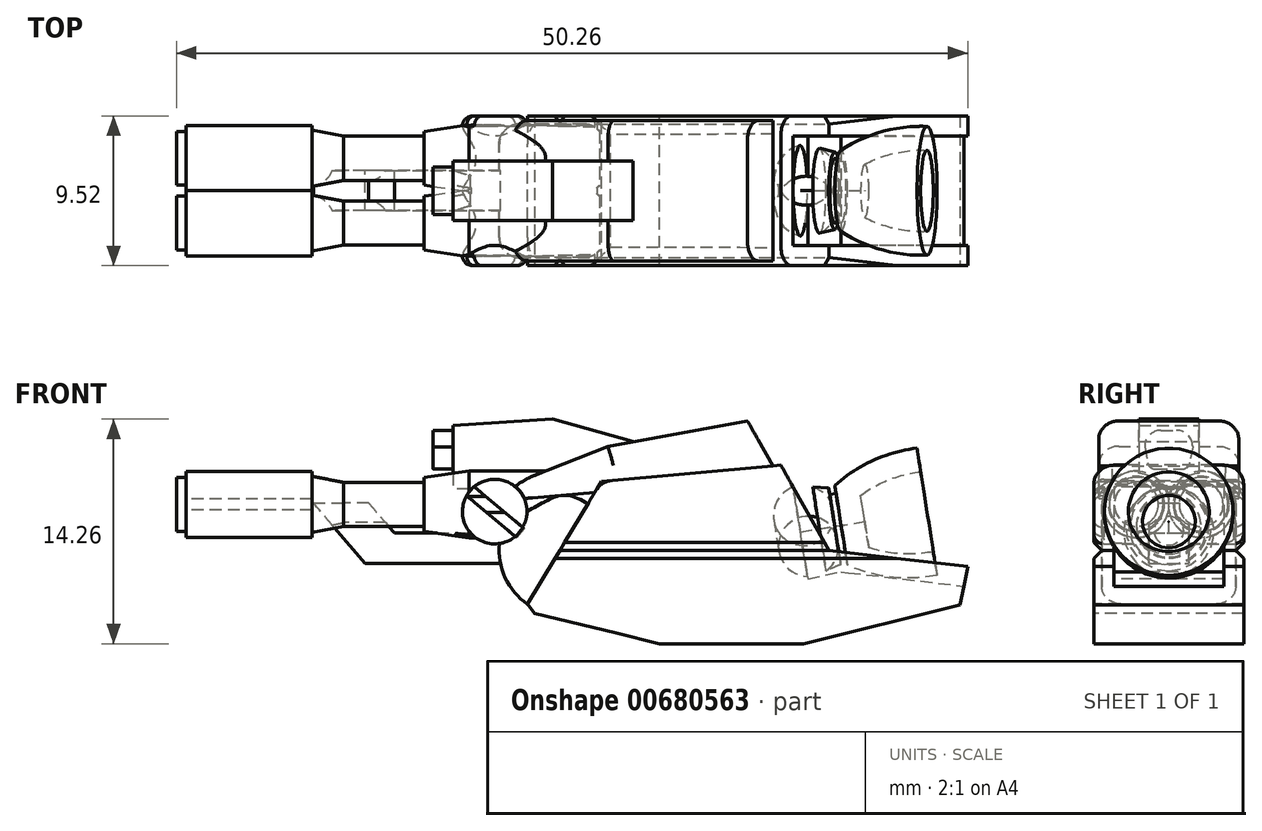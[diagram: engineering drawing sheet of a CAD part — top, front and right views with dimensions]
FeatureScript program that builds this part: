
annotation { "Feature Type Name" : "Feature", "Feature Type Description" : "" }
export const myFeature = defineFeature(function(context is Context, id is Id, definition is map)
    precondition{}
    {
        {
            var Q0;
            Q0=qCreatedBy(makeId("Front.planeOp"),FACE);
            var sketch = newSketch(context, id + "F0", { "sketchPlane" : qUnion([Q0])});
            skLineSegment(sketch, "E0", {"start": v(0, 0) * mm, "end": v(1.5, 0.24) * mm, "construction": true});
            skLineSegment(sketch, "E1", {"start": v(0, 0) * mm, "end": v(-2.23, 14.05) * mm, "construction": true});
            skLineSegment(sketch, "E2", {"start": v(5.05, 3.4) * mm, "end": v(4.82, 4.9) * mm});
            skLineSegment(sketch, "E3", {"start": v(-0.32, 2.02) * mm, "end": v(-0.4, 2.53) * mm});
            skArc(sketch, "E4", {"start": v(4.82, 4.9) * mm, "mid": v(2.02, 4.12) * mm, "end": v(-0.4, 2.53) * mm});
            skLineSegment(sketch, "E5", {"start": v(0, 0) * mm, "end": v(-19.66, -3.11) * mm, "construction": true});
            skLineSegment(sketch, "E6", {"start": v(-0.32, 2.02) * mm, "end": v(-0.72, 1.96) * mm});
            skLineSegment(sketch, "E7", {"start": v(-0.72, 1.96) * mm, "end": v(-0.79, 2.36) * mm});
            skLineSegment(sketch, "E8", {"start": v(-0.79, 2.36) * mm, "end": v(-1.8, 2.45) * mm});
            skLineSegment(sketch, "E9", {"start": v(-0.79, 2.36) * mm, "end": v(-6.83, 1.4) * mm, "construction": true});
            skLineSegment(sketch, "E10", {"start": v(-3.63, 6.1) * mm, "end": v(-2.98, 2.02) * mm, "construction": true});
            skLineSegment(sketch, "E11", {"start": v(-1.8, 2.45) * mm, "end": v(-3.02, 2.26) * mm, "construction": true});
            skPoint(sketch, "E12", {"position": v(-3.05, 2.42) * mm});
            skArc(sketch, "E13", {"start": v(-1.8, 2.45) * mm, "mid": v(-2.43, 2.54) * mm, "end": v(-3.05, 2.42) * mm});
            skLineSegment(sketch, "E14", {"start": v(-3.05, 2.42) * mm, "end": v(-2.6, -0.41) * mm});
            skLineSegment(sketch, "E15", {"start": v(-2.6, -0.41) * mm, "end": v(1.5, 0.24) * mm});
            skArc(sketch, "E16", {"start": v(5.05, 3.4) * mm, "mid": v(3.05, 2.9) * mm, "end": v(1.24, 1.9) * mm});
            skLineSegment(sketch, "E17", {"start": v(1.24, 1.9) * mm, "end": v(1.5, 0.24) * mm});
            skLineSegment(sketch, "E18.trimOffspring", {"start": v(5.46, 0.86) * mm, "end": v(24.57, 3.9) * mm, "construction": true});
            skSolve(sketch);
        }
        {
            var Q0;
            Q0=makeQuery(id+"F0.imprint","IMPRINT",FACE,{"disambiguationData":[TD([[makeQuery(id+"F0.imprint","IMPRINT",EDGE,{"derivedFrom":sQuery(id+"F0.wireOp",EDGE,"E2")}),1.0]])]});
            var Q1;
            Q1=sQuery(id+"F0.wireOp",EDGE,"E5");
            revolve(context, id + "F1", {"entities" : qUnion([Q0]), "axis" : qUnion([Q1]), "revolveType" : RevolveType.FULL});
        }
        {
            var Q0;
            Q0=qCreatedBy(makeId("Front.planeOp"),FACE);
            var sketch = newSketch(context, id + "F2", { "sketchPlane" : qUnion([Q0])});
            skLineSegment(sketch, "E19", {"start": v(0, 0) * mm, "end": v(1.56, -9.86) * mm, "construction": true});
            skLineSegment(sketch, "E20", {"start": v(0.48, -3.01) * mm, "end": v(7.8, -3.87) * mm});
            skLineSegment(sketch, "E21", {"start": v(7.8, -3.87) * mm, "end": v(7.55, -5.07) * mm});
            skLineSegment(sketch, "E22", {"start": v(7.55, -5.07) * mm, "end": v(-2.39, -7.52) * mm});
            skLineSegment(sketch, "E23", {"start": v(-2.39, -7.52) * mm, "end": v(-14.3, -6.85) * mm});
            skLineSegment(sketch, "E24", {"start": v(-15.66, 2.07) * mm, "end": v(-15.25, 2.78) * mm});
            skLineSegment(sketch, "E25", {"start": v(-15.25, 2.78) * mm, "end": v(-3.83, 3.82) * mm});
            skLineSegment(sketch, "E26", {"start": v(0.48, -3.01) * mm, "end": v(0, -2.95) * mm});
            skLineSegment(sketch, "E27", {"start": v(-3.83, 3.82) * mm, "end": v(-3.05, 2.44) * mm});
            skLineSegment(sketch, "E28", {"start": v(0, -2.95) * mm, "end": v(-50.8, -2.95) * mm, "construction": true});
            skLineSegment(sketch, "E29", {"start": v(-19.92, -5) * mm, "end": v(-19.48, -5.6) * mm});
            skLineSegment(sketch, "E30", {"start": v(-19.48, -5.6) * mm, "end": v(-14.3, -6.85) * mm});
            skLineSegment(sketch, "E31", {"start": v(-3.05, 2.44) * mm, "end": v(-2.12, -3.4) * mm});
            skLineSegment(sketch, "E32", {"start": v(-2.12, -3.4) * mm, "end": v(0, -2.95) * mm});
            skLineSegment(sketch, "E33", {"start": v(-2.12, -3.4) * mm, "end": v(-2.12, 15.55) * mm, "construction": true});
            skLineSegment(sketch, "E34", {"start": v(-15.66, 2.07) * mm, "end": v(-19.92, -5) * mm});
            skPoint(sketch, "E35.end.orphan", {"position": v(-34.01, 0.4) * mm});
            skPoint(sketch, "E36.orphan", {"position": v(-35.04, -0.28) * mm});
            skPoint(sketch, "E37.start.orphan", {"position": v(-32.58, -4.06) * mm});
            skSolve(sketch);
        }
        {
            var Q0;
            Q0=qSketchRegion(id+"F2",true);
            extrude(context, id + "F3", {"entities" : qUnion([Q0]), "operationType" : NewBodyOperationType.ADD, "endBound" : BoundingType.SYMMETRIC, "oppositeDirection" : true, "depth" : 9.52 * mm, "offsetDistance" : 25.4 * mm});
        }
        {
            var Q0;
            Q0=makeQuery(id+"F3.opExtrude","CAP_FACE",FACE,{"disambiguationData":[OSD([sQuery(id+"F2.wireOp",EDGE,"E20"),sQuery(id+"F2.wireOp",EDGE,"E21"),sQuery(id+"F2.wireOp",EDGE,"E22"),sQuery(id+"F2.wireOp",EDGE,"E23"),sQuery(id+"F2.wireOp",EDGE,"6j32zmyG-TKOO-vOuO-Pmrx-HYvCCri2Y5XP"),sQuery(id+"F2.wireOp",EDGE,"E37"),sQuery(id+"F2.wireOp",EDGE,"E35"),sQuery(id+"F2.wireOp",EDGE,"kUpx39iX-orTo-v9rc-2KpO-4MKOgX1ehOD6"),sQuery(id+"F2.wireOp",EDGE,"E24"),sQuery(id+"F2.wireOp",EDGE,"E25"),sQuery(id+"F2.wireOp",EDGE,"E26"),sQuery(id+"F2.wireOp",EDGE,"E27"),sQuery(id+"F2.wireOp",EDGE,"E29"),sQuery(id+"F2.wireOp",EDGE,"E30"),sQuery(id+"F2.wireOp",EDGE,"E31"),sQuery(id+"F2.wireOp",EDGE,"E32")])],"isStart":true});
            var sketch = newSketch(context, id + "F4", { "sketchPlane" : qUnion([Q0])});
            skLineSegment(sketch, "E38", {"start": v(7.8, -3.87) * mm, "end": v(8.05, -2.62) * mm});
            skLineSegment(sketch, "E39", {"start": v(8.05, -2.62) * mm, "end": v(-0.77, -1.59) * mm});
            skLineSegment(sketch, "E40", {"start": v(-3.05, 2.44) * mm, "end": v(-2.12, -3.4) * mm});
            skLineSegment(sketch, "E41", {"start": v(-2.12, -3.4) * mm, "end": v(0, -2.95) * mm});
            skLineSegment(sketch, "E42", {"start": v(0, -2.95) * mm, "end": v(7.8, -3.87) * mm});
            skLineSegment(sketch, "E43", {"start": v(-3.05, 2.44) * mm, "end": v(0, -2.95) * mm, "construction": true});
            skLineSegment(sketch, "E44", {"start": v(-3.05, 2.44) * mm, "end": v(-0.77, -1.59) * mm});
            skSolve(sketch);
        }
        {
            var Q0;
            Q0=qSketchRegion(id+"F4",true);
            extrude(context, id + "F5", {"entities" : qUnion([Q0]), "oppositeDirection" : true, "depth" : 1.27 * mm, "offsetDistance" : 25.4 * mm});
        }
        {
            var Q0;
            Q0=makeQuery(id+"F5.opExtrude","SWEPT_BODY",BODY,{"disambiguationData":[OSD([sQuery(id+"F4.wireOp",EDGE,"E38"),sQuery(id+"F4.wireOp",EDGE,"E39"),sQuery(id+"F4.wireOp",EDGE,"E40"),sQuery(id+"F4.wireOp",EDGE,"E41"),sQuery(id+"F4.wireOp",EDGE,"E42"),sQuery(id+"F4.wireOp",EDGE,"E44")])]});
            var Q1;
            Q1=qCreatedBy(makeId("Front.planeOp"),FACE);
            mirror(context, id + "F6", {"operationType" : NewBodyOperationType.ADD, "entities" : qUnion([Q0]), "mirrorPlane" : qUnion([Q1])});
        }
        {
            var Q0;
            Q0=qCreatedBy(makeId("Right.planeOp"),FACE);
            var sketch = newSketch(context, id + "F7", { "sketchPlane" : qUnion([Q0])});
            skLineSegment(sketch, "E45", {"start": v(-5.3, -1.59) * mm, "end": v(-3.08, -1.59) * mm, "construction": true});
            skLineSegment(sketch, "E46", {"start": v(-4.76, -1.53) * mm, "end": v(-4.76, -1.65) * mm, "construction": true});
            skLineSegment(sketch, "E47", {"start": v(-4.25, -1.59) * mm, "end": v(-4.82, -1.02) * mm});
            skLineSegment(sketch, "E48", {"start": v(-4.82, -1.02) * mm, "end": v(-4.82, -1.59) * mm});
            skLineSegment(sketch, "E49.MirrorCS", {"start": v(-4.82, -2.15) * mm, "end": v(-4.82, -1.59) * mm});
            skLineSegment(sketch, "E50.MirrorCS", {"start": v(-4.25, -1.59) * mm, "end": v(-4.82, -2.15) * mm});
            skLineSegment(sketch, "E51", {"start": v(0, 0) * mm, "end": v(0, -3.64) * mm, "construction": true});
            skLineSegment(sketch, "E52.MirrorCS", {"start": v(4.82, -1.02) * mm, "end": v(4.82, -1.59) * mm});
            skLineSegment(sketch, "E53.MirrorCS", {"start": v(4.82, -2.15) * mm, "end": v(4.82, -1.59) * mm});
            skLineSegment(sketch, "E54.MirrorCS", {"start": v(4.25, -1.59) * mm, "end": v(4.82, -2.15) * mm});
            skLineSegment(sketch, "E55.MirrorCS", {"start": v(4.25, -1.59) * mm, "end": v(4.82, -1.02) * mm});
            skSolve(sketch);
        }
        {
            var Q0;
            Q0=qSketchRegion(id+"F7",true);
            extrude(context, id + "F8", {"entities" : qUnion([Q0]), "operationType" : NewBodyOperationType.REMOVE, "endBound" : BoundingType.SYMMETRIC, "oppositeDirection" : true, "depth" : 50.8 * mm, "offsetDistance" : 25.4 * mm});
        }
        {
            var Q0;
            Q0=makeQuery(id+"F3.opExtrude","CAP_EDGE",EDGE,{"disambiguationData":[OSD([sQuery(id+"F2.wireOp",EDGE,"E25")])],"isStart":true});
            var Q1;
            Q1=makeQuery(id+"F3.opExtrude","CAP_EDGE",EDGE,{"disambiguationData":[OSD([sQuery(id+"F2.wireOp",EDGE,"E25")])],"isStart":false});
            var Q2;
            Q2=makeQuery(id+"F3.opExtrude","SWEPT_EDGE",EDGE,{"disambiguationData":[OSD([sQuery(id+"F2.wireOp",EDGE,"E24"),sQuery(id+"F2.wireOp",EDGE,"E25")])]});
            fillet(context, id + "F9", {"entities" : qUnion([Q0, Q1, Q2]), "radius" : 1.27 * mm, "tangentPropagation" : true, "allowEdgeOverflow" : false});
        }
        {
            var Q0;
            Q0=qCreatedBy(makeId("Front.planeOp"),FACE);
            var sketch = newSketch(context, id + "F10", { "sketchPlane" : qUnion([Q0])});
            skLineSegment(sketch, "E56", {"start": v(-19.78, 2.37) * mm, "end": v(0, 4.17) * mm, "construction": true});
            skPoint(sketch, "E57", {"position": v(-3.83, 3.82) * mm});
            skLineSegment(sketch, "E58", {"start": v(-4.72, 5.39) * mm, "end": v(1.35, -5.34) * mm, "construction": true});
            skLineSegment(sketch, "E59", {"start": v(-4.33, 3.77) * mm, "end": v(-5.95, 6.63) * mm});
            skLineSegment(sketch, "E60", {"start": v(-5.95, 6.63) * mm, "end": v(-14.81, 5.02) * mm});
            skLineSegment(sketch, "E61", {"start": v(-14.81, 5.02) * mm, "end": v(-20.9, 2.6) * mm});
            skArc(sketch, "E62", {"start": v(-20.12, 1.7) * mm, "mid": v(-20.43, 2.22) * mm, "end": v(-20.9, 2.6) * mm});
            skLineSegment(sketch, "E63", {"start": v(-20.12, 1.7) * mm, "end": v(-15.64, 2.1) * mm});
            skLineSegment(sketch, "E64", {"start": v(-15.23, 2.78) * mm, "end": v(-4.33, 3.77) * mm});
            skLineSegment(sketch, "E65", {"start": v(-15.64, 2.1) * mm, "end": v(-15.23, 2.78) * mm});
            skSolve(sketch);
        }
        {
            var Q0;
            Q0 = qSketchRegion(id + "F10", true);
            extrude(context, id + "F11", {"entities" : qUnion([Q0]), "operationType" : NewBodyOperationType.ADD, "endBound" : BoundingType.SYMMETRIC, "depth" : 8.9 * mm, "offsetDistance" : 25.4 * mm});
        }
        {
            var Q0;
            Q0=makeQuery(id+"F11.opExtrude","CAP_EDGE",EDGE,{"disambiguationData":[OSD([sQuery(id+"F10.wireOp",EDGE,"E60")])],"isStart":false});
            var Q1;
            Q1=makeQuery(id+"F11.opExtrude","CAP_EDGE",EDGE,{"disambiguationData":[OSD([sQuery(id+"F10.wireOp",EDGE,"E61")])],"isStart":false});
            var Q2;
            Q2=makeQuery(id+"F11.opExtrude","CAP_EDGE",EDGE,{"disambiguationData":[OSD([sQuery(id+"F10.wireOp",EDGE,"E61")])],"isStart":true});
            var Q3;
            Q3=makeQuery(id+"F11.opExtrude","CAP_EDGE",EDGE,{"disambiguationData":[OSD([sQuery(id+"F10.wireOp",EDGE,"E60")])],"isStart":true});
            fillet(context, id + "F12", {"entities" : qUnion([Q0, Q1, Q2, Q3]), "radius" : 1.27 * mm, "tangentPropagation" : true, "allowEdgeOverflow" : false});
        }
        {
            var Q0;
            Q0=qCreatedBy(makeId("Front.planeOp"),FACE);
            var sketch = newSketch(context, id + "F13", { "sketchPlane" : qUnion([Q0])});
            skCircle(sketch, "E66", {"center": v(-22, 0.87) * mm, "radius": 2.05 * mm});
            skSolve(sketch);
        }
        {
            var Q0;
            Q0 = qSketchRegion(id + "F13", true);
            extrude(context, id + "F14", {"entities" : qUnion([Q0]), "operationType" : NewBodyOperationType.ADD, "endBound" : BoundingType.SYMMETRIC, "depth" : 9.52 * mm, "offsetDistance" : 25.4 * mm});
        }
        {
            var Q0;
            Q0=qCreatedBy(makeId("Front.planeOp"),FACE);
            var sketch = newSketch(context, id + "F15", { "sketchPlane" : qUnion([Q0])});
            skCircle(sketch, "E67", {"center": v(-17.56, -1.58) * mm, "radius": 4.16 * mm});
            skSolve(sketch);
        }
        {
            var Q0;
            Q0=makeQuery(id+"F15.imprint","IMPRINT",FACE,{"disambiguationData":[TD([[makeQuery(id+"F15.imprint","IMPRINT",EDGE,{"derivedFrom":sQuery(id+"F15.wireOp",EDGE,"E67")}),1.0]])]});
            extrude(context, id + "F16", {"entities" : qUnion([Q0]), "endBound" : BoundingType.SYMMETRIC, "depth" : 8.5 * mm, "offsetDistance" : 25.4 * mm});
        }
        {
            var Q0;
            Q0=makeQuery(id+"F16.opExtrude","CAP_EDGE",EDGE,{"disambiguationData":[OSD([sQuery(id+"F15.wireOp",EDGE,"E67")])],"isStart":true});
            var Q1;
            Q1=makeQuery(id+"F16.opExtrude","CAP_EDGE",EDGE,{"disambiguationData":[OSD([sQuery(id+"F15.wireOp",EDGE,"E67")])],"isStart":false});
            fillet(context, id + "F17", {"entities" : qUnion([Q0, Q1]), "radius" : 1.27 * mm, "tangentPropagation" : true, "allowEdgeOverflow" : false});
        }
        {
            var Q0;
            Q0=makeQuery(id+"F14.opExtrude","CAP_EDGE",EDGE,{"disambiguationData":[OSD([sQuery(id+"F13.wireOp",EDGE,"E66")])],"isStart":false});
            var Q1;
            Q1=makeQuery(id+"F14.opExtrude","CAP_EDGE",EDGE,{"disambiguationData":[OSD([sQuery(id+"F13.wireOp",EDGE,"E66")])],"isStart":true});
            fillet(context, id + "F18", {"entities" : qUnion([Q0, Q1]), "radius" : 0.64 * mm, "tangentPropagation" : true, "allowEdgeOverflow" : false});
        }
        {
            var Q0;
            Q0=makeQuery(id+"F14.opExtrude","CAP_FACE",FACE,{"disambiguationData":[OSD([sQuery(id+"F13.wireOp",EDGE,"E66")])],"isStart":false});
            var sketch = newSketch(context, id + "F19", { "sketchPlane" : qUnion([Q0])});
            skLineSegment(sketch, "E68", {"start": v(-22, 0.87) * mm, "end": v(-25.8, 4.06) * mm, "construction": true});
            skLineSegment(sketch, "E69", {"start": v(-23.6, 2.7) * mm, "end": v(-20.19, -0.15) * mm});
            skLineSegment(sketch, "E70", {"start": v(-23.6, 2.7) * mm, "end": v(-23.84, 2.42) * mm});
            skLineSegment(sketch, "E71.MirrorCS", {"start": v(-24.08, 2.13) * mm, "end": v(-23.84, 2.42) * mm});
            skLineSegment(sketch, "E72.MirrorCS", {"start": v(-24.08, 2.13) * mm, "end": v(-20.67, -0.73) * mm});
            skLineSegment(sketch, "E73", {"start": v(-20.67, -0.73) * mm, "end": v(-20.19, -0.15) * mm});
            skSolve(sketch);
        }
        {
            var Q0;
            Q0 = qSketchRegion(id + "F19", true);
            extrude(context, id + "F20", {"entities" : qUnion([Q0]), "operationType" : NewBodyOperationType.REMOVE, "oppositeDirection" : true, "depth" : 0.64 * mm, "offsetDistance" : 25.4 * mm});
        }
        {
            var Q0;
            Q0=qCreatedBy(makeId("Front.planeOp"),FACE);
            var sketch = newSketch(context, id + "F21", { "sketchPlane" : qUnion([Q0])});
            skLineSegment(sketch, "E74", {"start": v(-20.66, 2.66) * mm, "end": v(-21.29, 2.52) * mm});
            skLineSegment(sketch, "E75", {"start": v(-21.29, 2.52) * mm, "end": v(-20.29, 1.58) * mm});
            skLineSegment(sketch, "E76", {"start": v(-20.29, 1.58) * mm, "end": v(-19.87, 1.87) * mm});
            skLineSegment(sketch, "E77", {"start": v(-19.87, 1.87) * mm, "end": v(-20.66, 2.66) * mm});
            skSolve(sketch);
        }
        {
            var Q0;
            Q0 = qSketchRegion(id + "F21", true);
            extrude(context, id + "F22", {"entities" : qUnion([Q0]), "endBound" : BoundingType.SYMMETRIC, "depth" : 6.35 * mm, "offsetDistance" : 25.4 * mm});
        }
        {
            var Q0;
            Q0=qCreatedBy(makeId("Front.planeOp"),FACE);
            var sketch = newSketch(context, id + "F23", { "sketchPlane" : qUnion([Q0])});
            skLineSegment(sketch, "E78", {"start": v(-13.2, 5.31) * mm, "end": v(-18.33, 6.74) * mm});
            skLineSegment(sketch, "E79", {"start": v(-18.33, 6.74) * mm, "end": v(-24.66, 6.33) * mm});
            skLineSegment(sketch, "E80", {"start": v(-24.66, 6.33) * mm, "end": v(-24.66, 6.03) * mm});
            skLineSegment(sketch, "E81", {"start": v(-24.66, 6.03) * mm, "end": v(-25.9, 6.03) * mm});
            skLineSegment(sketch, "E82", {"start": v(-25.9, 6.03) * mm, "end": v(-25.9, 3.57) * mm});
            skLineSegment(sketch, "E83", {"start": v(-25.9, 3.57) * mm, "end": v(-24.66, 3.57) * mm});
            skLineSegment(sketch, "E84", {"start": v(-24.66, 3.57) * mm, "end": v(-24.66, 2.3) * mm});
            skLineSegment(sketch, "E85", {"start": v(-24.66, 2.3) * mm, "end": v(-21.67, 2.3) * mm});
            skLineSegment(sketch, "E86", {"start": v(-13.2, 5.31) * mm, "end": v(-21.67, 2.3) * mm});
            skSolve(sketch);
        }
        {
            var Q0;
            Q0 = qSketchRegion(id + "F23", true);
            extrude(context, id + "F24", {"entities" : qUnion([Q0]), "endBound" : BoundingType.SYMMETRIC, "depth" : 3.8 * mm, "offsetDistance" : 25.4 * mm});
        }
        {
            var Q0;
            Q0=makeQuery(id+"F24.opExtrude","SWEPT_FACE",FACE,{"disambiguationData":[OSD([sQuery(id+"F23.wireOp",EDGE,"E84")])]});
            var sketch = newSketch(context, id + "F25", { "sketchPlane" : qUnion([Q0])});
            skLineSegment(sketch, "E87", {"start": v(0, 6.62) * mm, "end": v(0, 3.27) * mm, "construction": true});
            skPoint(sketch, "E87.endSnap0", {"position": v(0, 3.57) * mm});
            skLineSegment(sketch, "E88.bottom", {"start": v(-1.52, 6.57) * mm, "end": v(-2.08, 6.57) * mm});
            skLineSegment(sketch, "E88.top", {"start": v(-1.52, 3.48) * mm, "end": v(-2.08, 3.48) * mm});
            skLineSegment(sketch, "E88.left", {"start": v(-1.52, 6.57) * mm, "end": v(-1.52, 3.48) * mm});
            skLineSegment(sketch, "E88.right", {"start": v(-2.08, 6.57) * mm, "end": v(-2.08, 3.48) * mm});
            skLineSegment(sketch, "E89.MirrorCS", {"start": v(1.52, 6.57) * mm, "end": v(2.08, 6.57) * mm});
            skLineSegment(sketch, "E90.MirrorCS", {"start": v(1.52, 6.57) * mm, "end": v(1.52, 3.48) * mm});
            skLineSegment(sketch, "E91.MirrorCS", {"start": v(2.08, 6.57) * mm, "end": v(2.08, 3.48) * mm});
            skLineSegment(sketch, "E92.MirrorCS", {"start": v(1.52, 3.48) * mm, "end": v(2.08, 3.48) * mm});
            skSolve(sketch);
        }
        {
            var Q0;
            Q0 = qSketchRegion(id + "F25", true);
            extrude(context, id + "F26", {"entities" : qUnion([Q0]), "operationType" : NewBodyOperationType.REMOVE, "endBound" : BoundingType.THROUGH_ALL, "depth" : 25.4 * mm, "offsetDistance" : 25.4 * mm});
        }
        {
            var Q0;
            Q0=makeQuery(id+"F26.boolean.opBoolean","INTERSECT",EDGE,{"derivedFrom":[makeQuery(id+"F24.opExtrude","SWEPT_FACE",FACE,{"disambiguationData":[OSD([sQuery(id+"F23.wireOp",EDGE,"E81")])]}),makeQuery(id+"F26.opExtrude","SWEPT_FACE",FACE,{"disambiguationData":[OSD([sQuery(id+"F25.wireOp",EDGE,"E88.left")])]})]});
            var Q1;
            Q1=makeQuery(id+"F26.boolean.opBoolean","INTERSECT",EDGE,{"derivedFrom":[makeQuery(id+"F24.opExtrude","SWEPT_FACE",FACE,{"disambiguationData":[OSD([sQuery(id+"F23.wireOp",EDGE,"E81")])]}),makeQuery(id+"F26.opExtrude","SWEPT_FACE",FACE,{"disambiguationData":[OSD([sQuery(id+"F25.wireOp",EDGE,"E90.MirrorCS")])]})]});
            fillet(context, id + "F27", {"entities" : qUnion([Q0, Q1]), "radius" : 1.02 * mm, "tangentPropagation" : true, "allowEdgeOverflow" : false});
        }
        {
            var Q0;
            Q0=makeQuery(id+"F26.boolean.opBoolean","INTERSECT",EDGE,{"derivedFrom":[makeQuery(id+"F24.opExtrude","SWEPT_FACE",FACE,{"disambiguationData":[OSD([sQuery(id+"F23.wireOp",EDGE,"E83")])]}),makeQuery(id+"F26.opExtrude","SWEPT_FACE",FACE,{"disambiguationData":[OSD([sQuery(id+"F25.wireOp",EDGE,"E88.left")])]})]});
            var Q1;
            Q1=makeQuery(id+"F26.boolean.opBoolean","INTERSECT",EDGE,{"derivedFrom":[makeQuery(id+"F24.opExtrude","SWEPT_FACE",FACE,{"disambiguationData":[OSD([sQuery(id+"F23.wireOp",EDGE,"E83")])]}),makeQuery(id+"F26.opExtrude","SWEPT_FACE",FACE,{"disambiguationData":[OSD([sQuery(id+"F25.wireOp",EDGE,"E90.MirrorCS")])]})]});
            chamfer(context, id + "F28", {"entities" : qUnion([Q0, Q1]), "chamferType" : ChamferType.TWO_OFFSETS, "width1" : 0.25 * mm, "oppositeDirection" : false, "width2" : 1.4 * mm, "tangentPropagation" : true});
        }
        {
            var Q0;
            {var subQ0=makeQuery(id+"F24.opExtrude","SWEPT_FACE",FACE,{"disambiguationData":[OSD([sQuery(id+"F23.wireOp",EDGE,"E83")])]});Q0=makeQuery(id+"F28.opChamfer","BLEND_EDGE",EDGE,{"blendedFrom":[makeQuery(id+"F26.boolean.opBoolean","INTERSECT",EDGE,{"derivedFrom":[subQ0,makeQuery(id+"F26.opExtrude","SWEPT_FACE",FACE,{"disambiguationData":[OSD([sQuery(id+"F25.wireOp",EDGE,"E88.left")])]})]}),subQ0],"blendedInto":[subQ0]});}
            var Q1;
            {var subQ0=makeQuery(id+"F24.opExtrude","SWEPT_FACE",FACE,{"disambiguationData":[OSD([sQuery(id+"F23.wireOp",EDGE,"E83")])]});Q1=makeQuery(id+"F28.opChamfer","BLEND_EDGE",EDGE,{"blendedFrom":[makeQuery(id+"F26.boolean.opBoolean","INTERSECT",EDGE,{"derivedFrom":[subQ0,makeQuery(id+"F26.opExtrude","SWEPT_FACE",FACE,{"disambiguationData":[OSD([sQuery(id+"F25.wireOp",EDGE,"E90.MirrorCS")])]})]}),subQ0],"blendedInto":[subQ0]});}
            fillet(context, id + "F29", {"entities" : qUnion([Q0, Q1]), "radius" : 0.5 * mm, "tangentPropagation" : true, "allowEdgeOverflow" : false});
        }
        {
            var Q0;
            Q0=qCreatedBy(makeId("Front.planeOp"),FACE);
            cPlane(context, id + "F30", {"entities" : qUnion([Q0]), "cplaneType" : CPlaneType.OFFSET, "offset" : 2.06 * mm, "width" : 152.4 * mm, "height" : 152.4 * mm});
        }
        {
            var Q0;
            Q0=makeQuery(id+"F14.opExtrude","CAP_FACE",FACE,{"disambiguationData":[OSD([sQuery(id+"F13.wireOp",EDGE,"E66")])],"isStart":true});
            var sketch = newSketch(context, id + "F31", { "sketchPlane" : qUnion([Q0])});
            skLineSegment(sketch, "E93", {"start": v(22, 0.87) * mm, "end": v(25.36, 3.7) * mm, "construction": true});
            skLineSegment(sketch, "E94", {"start": v(23.43, 2.57) * mm, "end": v(23.67, 2.28) * mm});
            skPoint(sketch, "E94.endSnap0", {"position": v(23.67, 2.28) * mm});
            skLineSegment(sketch, "E95", {"start": v(23.43, 2.57) * mm, "end": v(20.14, -0.19) * mm});
            skLineSegment(sketch, "E96.MirrorCS", {"start": v(23.92, 1.99) * mm, "end": v(20.63, -0.77) * mm});
            skLineSegment(sketch, "E97.MirrorCS", {"start": v(23.92, 1.99) * mm, "end": v(23.67, 2.28) * mm});
            skLineSegment(sketch, "E98", {"start": v(20.14, -0.19) * mm, "end": v(20.63, -0.77) * mm});
            skSolve(sketch);
        }
        {
            var Q0;
            Q0 = qSketchRegion(id + "F31", true);
            extrude(context, id + "F32", {"entities" : qUnion([Q0]), "operationType" : NewBodyOperationType.REMOVE, "oppositeDirection" : true, "depth" : 0.64 * mm, "offsetDistance" : 25.4 * mm});
        }
        {
            var Q0;
            Q0=qCreatedBy(id+"F30.planeOp",FACE);
            var sketch = newSketch(context, id + "F33", { "sketchPlane" : qUnion([Q0])});
            skLineSegment(sketch, "E99", {"start": v(-15.34, 3.45) * mm, "end": v(-23.64, 3.45) * mm});
            skLineSegment(sketch, "E100", {"start": v(-23.64, 3.45) * mm, "end": v(-26.48, 3.04) * mm});
            skLineSegment(sketch, "E101", {"start": v(-26.48, 3.04) * mm, "end": v(-26.48, 2.73) * mm});
            skLineSegment(sketch, "E102", {"start": v(-26.48, 2.73) * mm, "end": v(-31.6, 2.73) * mm});
            skLineSegment(sketch, "E103", {"start": v(-31.6, 2.73) * mm, "end": v(-33.6, 3.11) * mm});
            skLineSegment(sketch, "E104", {"start": v(-33.6, 3.11) * mm, "end": v(-33.6, 3.42) * mm});
            skLineSegment(sketch, "E105", {"start": v(-33.6, 3.42) * mm, "end": v(-41.6, 3.42) * mm});
            skLineSegment(sketch, "E106", {"start": v(-41.6, 3.42) * mm, "end": v(-41.6, 3.04) * mm});
            skLineSegment(sketch, "E107", {"start": v(-41.6, 3.04) * mm, "end": v(-42.21, 3.04) * mm});
            skLineSegment(sketch, "E108", {"start": v(-42.21, 3.04) * mm, "end": v(-42.21, 1.33) * mm});
            skLineSegment(sketch, "E109", {"start": v(-42.21, 1.33) * mm, "end": v(-15.34, 1.33) * mm});
            skLineSegment(sketch, "E110", {"start": v(-15.34, 1.33) * mm, "end": v(-15.34, 3.45) * mm});
            skPoint(sketch, "E111.orphan", {"position": v(-15.34, 3.45) * mm});
            skPoint(sketch, "E112.orphan", {"position": v(-15.34, 4) * mm});
            skSolve(sketch);
        }
        {
            var Q0;
            Q0 = qSketchRegion(id + "F33", true);
            var Q1;
            Q1=sQuery(id+"F33.wireOp",EDGE,"E109");
            revolve(context, id + "F34", {"entities" : qUnion([Q0]), "axis" : qUnion([Q1]), "revolveType" : RevolveType.FULL});
        }
        {
            var Q0;
            Q0=makeQuery(id+"F34.opRevolve","SWEPT_BODY",BODY,{"disambiguationData":[OSD([sQuery(id+"F33.wireOp",EDGE,"E99"),sQuery(id+"F33.wireOp",EDGE,"E100"),sQuery(id+"F33.wireOp",EDGE,"E101"),sQuery(id+"F33.wireOp",EDGE,"E102"),sQuery(id+"F33.wireOp",EDGE,"E103"),sQuery(id+"F33.wireOp",EDGE,"E104"),sQuery(id+"F33.wireOp",EDGE,"E105"),sQuery(id+"F33.wireOp",EDGE,"E106"),sQuery(id+"F33.wireOp",EDGE,"E107"),sQuery(id+"F33.wireOp",EDGE,"E108"),sQuery(id+"F33.wireOp",EDGE,"E109"),sQuery(id+"F33.wireOp",EDGE,"E110")])]});
            var Q1;
            Q1=qCreatedBy(makeId("Front.planeOp"),FACE);
            mirror(context, id + "F35", {"operationType" : NewBodyOperationType.ADD, "entities" : qUnion([Q0]), "mirrorPlane" : qUnion([Q1])});
        }
        {
            var Q0;
            Q0=qCreatedBy(makeId("Front.planeOp"),FACE);
            var sketch = newSketch(context, id + "F36", { "sketchPlane" : qUnion([Q0])});
            skLineSegment(sketch, "E113", {"start": v(-19.68, -2.42) * mm, "end": v(-30.24, -2.42) * mm});
            skLineSegment(sketch, "E114", {"start": v(-30.24, -2.42) * mm, "end": v(-33.52, 1.41) * mm});
            skLineSegment(sketch, "E115", {"start": v(-33.52, 1.41) * mm, "end": v(-30, 1.41) * mm});
            skLineSegment(sketch, "E116", {"start": v(-30, 1.41) * mm, "end": v(-28.36, -0.5) * mm});
            skPoint(sketch, "E116.endSnap0", {"position": v(-31.88, -0.5) * mm});
            skLineSegment(sketch, "E117", {"start": v(-28.36, -0.5) * mm, "end": v(-19.68, -0.5) * mm});
            skLineSegment(sketch, "E118", {"start": v(-19.68, -0.5) * mm, "end": v(-19.68, -2.42) * mm});
            skSolve(sketch);
        }
        {
            var Q0;
            Q0 = qSketchRegion(id + "F36", true);
            extrude(context, id + "F37", {"entities" : qUnion([Q0]), "operationType" : NewBodyOperationType.ADD, "endBound" : BoundingType.SYMMETRIC, "depth" : 2.54 * mm, "offsetDistance" : 25.4 * mm});
        }
        {
            var Q0;
            Q0=qCreatedBy(makeId("Front.planeOp"),FACE);
            var sketch = newSketch(context, id + "F38", { "sketchPlane" : qUnion([Q0])});
            skLineSegment(sketch, "E119", {"start": v(-14.3, -6.85) * mm, "end": v(-11.53, -7.52) * mm});
            skLineSegment(sketch, "E120", {"start": v(-11.53, -7.52) * mm, "end": v(-2.39, -7.52) * mm});
            skLineSegment(sketch, "E121", {"start": v(-14.3, -6.85) * mm, "end": v(-2.39, -7.52) * mm});
            skSolve(sketch);
        }
        {
            var Q0;
            Q0 = qSketchRegion(id + "F38", true);
            extrude(context, id + "F39", {"entities" : qUnion([Q0]), "operationType" : NewBodyOperationType.ADD, "endBound" : BoundingType.SYMMETRIC, "depth" : 9.52 * mm, "offsetDistance" : 25.4 * mm});
        }
    });
